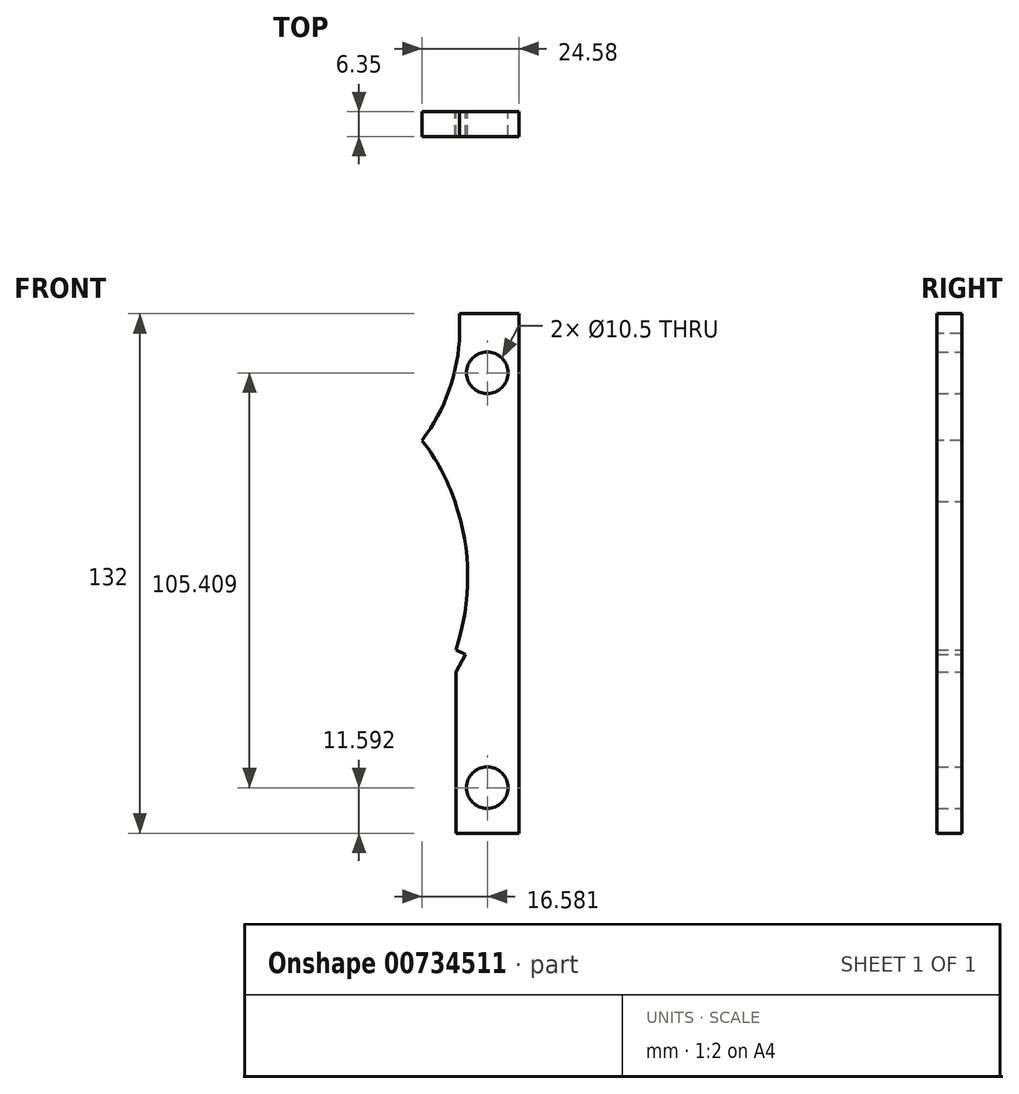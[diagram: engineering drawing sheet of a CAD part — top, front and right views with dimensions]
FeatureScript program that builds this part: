
annotation { "Feature Type Name" : "Feature", "Feature Type Description" : "" }
export const myFeature = defineFeature(function(context is Context, id is Id, definition is map)
    precondition{}
    {
        {
            var Q0;
            Q0=qCreatedBy(makeId("Front.planeOp"),FACE);
            var sketch = newSketch(context, id + "F0", { "sketchPlane" : qUnion([Q0])});
            skArc(sketch, "E0", {"start": v(-2.7, 61) * mm, "mid": v(-5.4, 46.65) * mm, "end": v(-12.3, 33.78) * mm});
            skArc(sketch, "E1", {"start": v(-12.3, 33.78) * mm, "mid": v(-7.43, 26.4) * mm, "end": v(-3.97, 18.25) * mm});
            skArc(sketch, "E2", {"start": v(-3.97, 18.25) * mm, "mid": v(-0.68, -0.55) * mm, "end": v(-3.7, -19.4) * mm});
            skLineSegment(sketch, "E3", {"start": v(-3.7, -19.4) * mm, "end": v(-1.2, -20.5) * mm});
            skLineSegment(sketch, "E4", {"start": v(-1.2, -20.5) * mm, "end": v(-3.7, -24.97) * mm});
            skLineSegment(sketch, "E5", {"start": v(-3.7, -24.97) * mm, "end": v(-3.7, -66) * mm});
            skLineSegment(sketch, "E6", {"start": v(-3.7, -66) * mm, "end": v(12.3, -66) * mm});
            skLineSegment(sketch, "E7", {"start": v(12.3, -66) * mm, "end": v(12.3, 66) * mm});
            skLineSegment(sketch, "E8", {"start": v(12.3, 66) * mm, "end": v(-2.7, 66) * mm});
            skLineSegment(sketch, "E9", {"start": v(-2.7, 66) * mm, "end": v(-2.7, 61) * mm});
            skCircle(sketch, "E10", {"center": v(4.3, 51) * mm, "radius": 5.25 * mm});
            skCircle(sketch, "E11", {"center": v(4.3, -54.4) * mm, "radius": 5.25 * mm});
            skSolve(sketch);
        }
        {
            var Q0;
            Q0 = qSketchRegion(id + "F0", true);
            extrude(context, id + "F1", {"entities" : qUnion([Q0]), "depth" : 6.35 * mm, "offsetDistance" : 25.4 * mm});
        }
    });
